# Revit family: 09800800
name_source: partatom
category: Specialty Equipment
units: mm (PartAtom-declared; Revit-internal decimal feet)

## family parameters
Always vertical = Yes
Cut with Voids When Loaded = No
Enable Cutting in Views = Yes
Maintain Annotation Orientation = No
OmniClass Number = 23.40.40.14
OmniClass Title = Food Service Equipment
Part Type = Normal
Room Calculation Point = No
Round Connector Dimension = Use Diameter
Shared = No
Work Plane-Based = No

## types (1)
- Standard
    Connector_3_Diameter = 24 mm  [stored 0.0787402 ft]
    Default Elevation = 0 mm  [stored 0 ft]
    Description = Varmeri RBVA-800
    Manufacturer = Rustfrie Bergh AS
    Model = 09800800
    URL = www.rustfriebergh.no/produkter/vannbad-varmeskap-varmeri/varmeri-rbva

note: [stored X ft] marks values corroborated as IEEE doubles in the binary element streams (Revit-internal decimal feet)

## geometry (parser evidence)
native form markers: Sweep x3
no freeform markers — native parametric forms only
